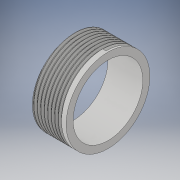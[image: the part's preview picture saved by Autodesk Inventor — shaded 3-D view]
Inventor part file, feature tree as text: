
AUTODESK INVENTOR PART (.ipt)
format: ipt  version: 2019 (Build 230136000, 136)  size: 1,038,848 bytes
history: native  units: mm
features: extrude x1, helix x1, sketch x1
ambient origin geometry x8: Origin, YZ Plane, XZ Plane, XY Plane, X Axis, Y Axis, Z Axis, Center Point
bodies: Body1 (feature_tree)
feature tree (3):
  extrude  "Extrusion2"  Depth=0.144333mm
  helix  "Coil1"  [1 undecoded]
  sketch  "Sketch2"  dims[d0=24.0mm d3=20.0mm d4=10.0mm d5=0.0mm d6=60.0deg d7=1.0mm d10=60.0deg d11=1.0mm d12=1.0mm d13=10.0mm d14=10.0mm d15=0.0mm d16=90.0deg d17=90.0deg d18=0.0mm d19=0.0mm d20=0.614mm d22=0.144333mm]
note: 1 required parameter value undecoded (feature->parameter linkage not recoverable at this tier; creation-order binding heuristic only, values carry confidence <= 0.55)
